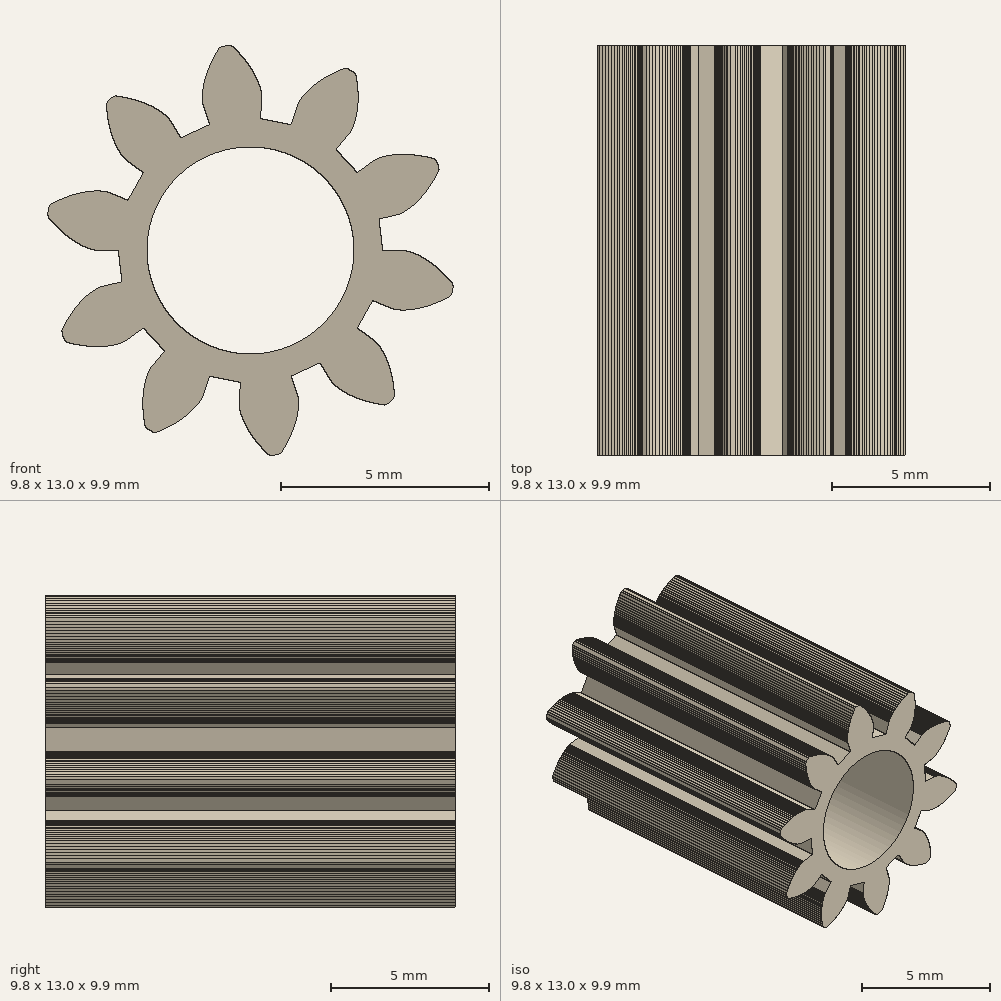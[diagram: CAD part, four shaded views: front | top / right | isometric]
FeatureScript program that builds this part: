
annotation { "Feature Type Name" : "Feature", "Feature Type Description" : "" }
export const myFeature = defineFeature(function(context is Context, id is Id, definition is map)
    precondition{}
    {
        {
            var Q0;
            Q0=qCreatedBy(makeId("Front.planeOp"),FACE);
            var sketch = newSketch(context, id + "F0", { "sketchPlane" : qUnion([Q0])});
            skCircle(sketch, "E0", {"center": v(0, 0) * mm, "radius": 2.5 * mm});
            skCircle(sketch, "E1", {"center": v(0, 0) * mm, "radius": 6 * mm});
            skLineSegment(sketch, "E2", {"start": v(3.6, 0.87) * mm, "end": v(3.1, 0.76) * mm});
            skLineSegment(sketch, "E3", {"start": v(3.6, 0.88) * mm, "end": v(3.6, 0.87) * mm});
            skLineSegment(sketch, "E4", {"start": v(3.6, 0.88) * mm, "end": v(3.6, 0.88) * mm});
            skLineSegment(sketch, "E5", {"start": v(3.62, 0.88) * mm, "end": v(3.6, 0.88) * mm});
            skLineSegment(sketch, "E6", {"start": v(3.63, 0.9) * mm, "end": v(3.62, 0.88) * mm});
            skLineSegment(sketch, "E7", {"start": v(3.65, 0.9) * mm, "end": v(3.63, 0.9) * mm});
            skLineSegment(sketch, "E8", {"start": v(3.68, 0.91) * mm, "end": v(3.65, 0.9) * mm});
            skLineSegment(sketch, "E9", {"start": v(3.7, 0.93) * mm, "end": v(3.68, 0.91) * mm});
            skLineSegment(sketch, "E10", {"start": v(3.74, 0.94) * mm, "end": v(3.7, 0.93) * mm});
            skLineSegment(sketch, "E11", {"start": v(3.77, 0.96) * mm, "end": v(3.74, 0.94) * mm});
            skLineSegment(sketch, "E12", {"start": v(3.8, 0.99) * mm, "end": v(3.77, 0.96) * mm});
            skLineSegment(sketch, "E13", {"start": v(3.85, 1.02) * mm, "end": v(3.8, 0.99) * mm});
            skLineSegment(sketch, "E14", {"start": v(3.9, 1.05) * mm, "end": v(3.85, 1.02) * mm});
            skLineSegment(sketch, "E15", {"start": v(3.94, 1.09) * mm, "end": v(3.9, 1.05) * mm});
            skLineSegment(sketch, "E16", {"start": v(3.98, 1.13) * mm, "end": v(3.94, 1.09) * mm});
            skLineSegment(sketch, "E17", {"start": v(4.03, 1.18) * mm, "end": v(3.98, 1.13) * mm});
            skLineSegment(sketch, "E18", {"start": v(4.08, 1.23) * mm, "end": v(4.03, 1.18) * mm});
            skLineSegment(sketch, "E19", {"start": v(4.14, 1.29) * mm, "end": v(4.08, 1.23) * mm});
            skLineSegment(sketch, "E20", {"start": v(4.19, 1.35) * mm, "end": v(4.14, 1.29) * mm});
            skLineSegment(sketch, "E21", {"start": v(4.24, 1.41) * mm, "end": v(4.19, 1.35) * mm});
            skLineSegment(sketch, "E22", {"start": v(4.3, 1.49) * mm, "end": v(4.24, 1.41) * mm});
            skLineSegment(sketch, "E23", {"start": v(4.35, 1.57) * mm, "end": v(4.3, 1.49) * mm});
            skLineSegment(sketch, "E24", {"start": v(4.4, 1.65) * mm, "end": v(4.35, 1.57) * mm});
            skLineSegment(sketch, "E25", {"start": v(4.45, 1.74) * mm, "end": v(4.4, 1.65) * mm});
            skLineSegment(sketch, "E26", {"start": v(4.5, 1.83) * mm, "end": v(4.45, 1.74) * mm});
            skLineSegment(sketch, "E27", {"start": v(4.55, 1.93) * mm, "end": v(4.5, 1.83) * mm});
            skLineSegment(sketch, "E28", {"start": v(4.55, 2.02) * mm, "end": v(4.55, 1.93) * mm});
            skLineSegment(sketch, "E29", {"start": v(4.48, 2.16) * mm, "end": v(4.55, 2.02) * mm});
            skLineSegment(sketch, "E30", {"start": v(4.42, 2.22) * mm, "end": v(4.48, 2.16) * mm});
            skLineSegment(sketch, "E31", {"start": v(4.31, 2.25) * mm, "end": v(4.42, 2.22) * mm});
            skLineSegment(sketch, "E32", {"start": v(4.2, 2.27) * mm, "end": v(4.31, 2.25) * mm});
            skLineSegment(sketch, "E33", {"start": v(4.1, 2.29) * mm, "end": v(4.2, 2.27) * mm});
            skLineSegment(sketch, "E34", {"start": v(4, 2.3) * mm, "end": v(4.1, 2.29) * mm});
            skLineSegment(sketch, "E35", {"start": v(3.91, 2.31) * mm, "end": v(4, 2.3) * mm});
            skLineSegment(sketch, "E36", {"start": v(3.82, 2.32) * mm, "end": v(3.91, 2.31) * mm});
            skLineSegment(sketch, "E37", {"start": v(3.74, 2.32) * mm, "end": v(3.82, 2.32) * mm});
            skLineSegment(sketch, "E38", {"start": v(3.66, 2.32) * mm, "end": v(3.74, 2.32) * mm});
            skLineSegment(sketch, "E39", {"start": v(3.58, 2.32) * mm, "end": v(3.66, 2.32) * mm});
            skLineSegment(sketch, "E40", {"start": v(3.5, 2.31) * mm, "end": v(3.58, 2.32) * mm});
            skLineSegment(sketch, "E41", {"start": v(3.44, 2.3) * mm, "end": v(3.5, 2.31) * mm});
            skLineSegment(sketch, "E42", {"start": v(3.38, 2.3) * mm, "end": v(3.44, 2.3) * mm});
            skLineSegment(sketch, "E43", {"start": v(3.32, 2.29) * mm, "end": v(3.38, 2.3) * mm});
            skLineSegment(sketch, "E44", {"start": v(3.27, 2.28) * mm, "end": v(3.32, 2.29) * mm});
            skLineSegment(sketch, "E45", {"start": v(3.22, 2.26) * mm, "end": v(3.27, 2.28) * mm});
            skLineSegment(sketch, "E46", {"start": v(3.18, 2.25) * mm, "end": v(3.22, 2.26) * mm});
            skLineSegment(sketch, "E47", {"start": v(3.14, 2.24) * mm, "end": v(3.18, 2.25) * mm});
            skLineSegment(sketch, "E48", {"start": v(3.1, 2.23) * mm, "end": v(3.14, 2.24) * mm});
            skLineSegment(sketch, "E49", {"start": v(3.07, 2.22) * mm, "end": v(3.1, 2.23) * mm});
            skLineSegment(sketch, "E50", {"start": v(3.05, 2.2) * mm, "end": v(3.07, 2.22) * mm});
            skLineSegment(sketch, "E51", {"start": v(3.03, 2.2) * mm, "end": v(3.05, 2.2) * mm});
            skLineSegment(sketch, "E52", {"start": v(3.01, 2.19) * mm, "end": v(3.03, 2.2) * mm});
            skLineSegment(sketch, "E53", {"start": v(3, 2.18) * mm, "end": v(3.01, 2.19) * mm});
            skLineSegment(sketch, "E54", {"start": v(3, 2.18) * mm, "end": v(3, 2.18) * mm});
            skLineSegment(sketch, "E55", {"start": v(3, 2.17) * mm, "end": v(3, 2.18) * mm});
            skLineSegment(sketch, "E56", {"start": v(2.58, 1.88) * mm, "end": v(3, 2.17) * mm});
            skLineSegment(sketch, "E57", {"start": v(2.07, 2.44) * mm, "end": v(2.58, 1.88) * mm});
            skLineSegment(sketch, "E58", {"start": v(2.4, 2.82) * mm, "end": v(2.07, 2.44) * mm});
            skLineSegment(sketch, "E59", {"start": v(2.4, 2.82) * mm, "end": v(2.4, 2.82) * mm});
            skLineSegment(sketch, "E60", {"start": v(2.4, 2.83) * mm, "end": v(2.4, 2.82) * mm});
            skLineSegment(sketch, "E61", {"start": v(2.4, 2.84) * mm, "end": v(2.4, 2.83) * mm});
            skLineSegment(sketch, "E62", {"start": v(2.42, 2.86) * mm, "end": v(2.4, 2.84) * mm});
            skLineSegment(sketch, "E63", {"start": v(2.43, 2.88) * mm, "end": v(2.42, 2.86) * mm});
            skLineSegment(sketch, "E64", {"start": v(2.44, 2.9) * mm, "end": v(2.43, 2.88) * mm});
            skLineSegment(sketch, "E65", {"start": v(2.45, 2.93) * mm, "end": v(2.44, 2.9) * mm});
            skLineSegment(sketch, "E66", {"start": v(2.47, 2.96) * mm, "end": v(2.45, 2.93) * mm});
            skLineSegment(sketch, "E67", {"start": v(2.48, 3) * mm, "end": v(2.47, 2.96) * mm});
            skLineSegment(sketch, "E68", {"start": v(2.5, 3.04) * mm, "end": v(2.48, 3) * mm});
            skLineSegment(sketch, "E69", {"start": v(2.52, 3.09) * mm, "end": v(2.5, 3.04) * mm});
            skLineSegment(sketch, "E70", {"start": v(2.53, 3.14) * mm, "end": v(2.52, 3.09) * mm});
            skLineSegment(sketch, "E71", {"start": v(2.55, 3.2) * mm, "end": v(2.53, 3.14) * mm});
            skLineSegment(sketch, "E72", {"start": v(2.56, 3.26) * mm, "end": v(2.55, 3.2) * mm});
            skLineSegment(sketch, "E73", {"start": v(2.57, 3.32) * mm, "end": v(2.56, 3.26) * mm});
            skLineSegment(sketch, "E74", {"start": v(2.58, 3.4) * mm, "end": v(2.57, 3.32) * mm});
            skLineSegment(sketch, "E75", {"start": v(2.59, 3.47) * mm, "end": v(2.58, 3.4) * mm});
            skLineSegment(sketch, "E76", {"start": v(2.6, 3.55) * mm, "end": v(2.59, 3.47) * mm});
            skLineSegment(sketch, "E77", {"start": v(2.6, 3.64) * mm, "end": v(2.6, 3.55) * mm});
            skLineSegment(sketch, "E78", {"start": v(2.6, 3.73) * mm, "end": v(2.6, 3.64) * mm});
            skLineSegment(sketch, "E79", {"start": v(2.6, 3.82) * mm, "end": v(2.6, 3.73) * mm});
            skLineSegment(sketch, "E80", {"start": v(2.6, 3.92) * mm, "end": v(2.6, 3.82) * mm});
            skLineSegment(sketch, "E81", {"start": v(2.58, 4.02) * mm, "end": v(2.6, 3.92) * mm});
            skLineSegment(sketch, "E82", {"start": v(2.57, 4.13) * mm, "end": v(2.58, 4.02) * mm});
            skLineSegment(sketch, "E83", {"start": v(2.55, 4.24) * mm, "end": v(2.57, 4.13) * mm});
            skLineSegment(sketch, "E84", {"start": v(2.5, 4.3) * mm, "end": v(2.55, 4.24) * mm});
            skLineSegment(sketch, "E85", {"start": v(2.35, 4.39) * mm, "end": v(2.5, 4.3) * mm});
            skLineSegment(sketch, "E86", {"start": v(2.27, 4.4) * mm, "end": v(2.35, 4.39) * mm});
            skLineSegment(sketch, "E87", {"start": v(2.17, 4.35) * mm, "end": v(2.27, 4.4) * mm});
            skLineSegment(sketch, "E88", {"start": v(2.07, 4.3) * mm, "end": v(2.17, 4.35) * mm});
            skLineSegment(sketch, "E89", {"start": v(1.98, 4.26) * mm, "end": v(2.07, 4.3) * mm});
            skLineSegment(sketch, "E90", {"start": v(1.89, 4.22) * mm, "end": v(1.98, 4.26) * mm});
            skLineSegment(sketch, "E91", {"start": v(1.8, 4.17) * mm, "end": v(1.89, 4.22) * mm});
            skLineSegment(sketch, "E92", {"start": v(1.73, 4.12) * mm, "end": v(1.8, 4.17) * mm});
            skLineSegment(sketch, "E93", {"start": v(1.66, 4.07) * mm, "end": v(1.73, 4.12) * mm});
            skLineSegment(sketch, "E94", {"start": v(1.6, 4.03) * mm, "end": v(1.66, 4.07) * mm});
            skLineSegment(sketch, "E95", {"start": v(1.53, 3.98) * mm, "end": v(1.6, 4.03) * mm});
            skLineSegment(sketch, "E96", {"start": v(1.48, 3.93) * mm, "end": v(1.53, 3.98) * mm});
            skLineSegment(sketch, "E97", {"start": v(1.43, 3.89) * mm, "end": v(1.48, 3.93) * mm});
            skLineSegment(sketch, "E98", {"start": v(1.38, 3.84) * mm, "end": v(1.43, 3.89) * mm});
            skLineSegment(sketch, "E99", {"start": v(1.34, 3.8) * mm, "end": v(1.38, 3.84) * mm});
            skLineSegment(sketch, "E100", {"start": v(1.3, 3.76) * mm, "end": v(1.34, 3.8) * mm});
            skLineSegment(sketch, "E101", {"start": v(1.27, 3.72) * mm, "end": v(1.3, 3.76) * mm});
            skLineSegment(sketch, "E102", {"start": v(1.25, 3.69) * mm, "end": v(1.27, 3.72) * mm});
            skLineSegment(sketch, "E103", {"start": v(1.22, 3.66) * mm, "end": v(1.25, 3.69) * mm});
            skLineSegment(sketch, "E104", {"start": v(1.2, 3.63) * mm, "end": v(1.22, 3.66) * mm});
            skLineSegment(sketch, "E105", {"start": v(1.18, 3.6) * mm, "end": v(1.2, 3.63) * mm});
            skLineSegment(sketch, "E106", {"start": v(1.17, 3.58) * mm, "end": v(1.18, 3.6) * mm});
            skLineSegment(sketch, "E107", {"start": v(1.16, 3.56) * mm, "end": v(1.17, 3.58) * mm});
            skLineSegment(sketch, "E108", {"start": v(1.15, 3.54) * mm, "end": v(1.16, 3.56) * mm});
            skLineSegment(sketch, "E109", {"start": v(1.15, 3.53) * mm, "end": v(1.15, 3.54) * mm});
            skLineSegment(sketch, "E110", {"start": v(1.14, 3.52) * mm, "end": v(1.15, 3.53) * mm});
            skLineSegment(sketch, "E111", {"start": v(1.14, 3.52) * mm, "end": v(1.14, 3.52) * mm});
            skLineSegment(sketch, "E112", {"start": v(0.99, 3.04) * mm, "end": v(1.14, 3.52) * mm});
            skLineSegment(sketch, "E113", {"start": v(0.24, 3.18) * mm, "end": v(0.99, 3.04) * mm});
            skLineSegment(sketch, "E114", {"start": v(0.28, 3.69) * mm, "end": v(0.24, 3.18) * mm});
            skLineSegment(sketch, "E115", {"start": v(0.28, 3.7) * mm, "end": v(0.28, 3.69) * mm});
            skLineSegment(sketch, "E116", {"start": v(0.28, 3.7) * mm, "end": v(0.28, 3.7) * mm});
            skLineSegment(sketch, "E117", {"start": v(0.28, 3.71) * mm, "end": v(0.28, 3.7) * mm});
            skLineSegment(sketch, "E118", {"start": v(0.28, 3.73) * mm, "end": v(0.28, 3.71) * mm});
            skLineSegment(sketch, "E119", {"start": v(0.27, 3.75) * mm, "end": v(0.28, 3.73) * mm});
            skLineSegment(sketch, "E120", {"start": v(0.27, 3.78) * mm, "end": v(0.27, 3.75) * mm});
            skLineSegment(sketch, "E121", {"start": v(0.27, 3.81) * mm, "end": v(0.27, 3.78) * mm});
            skLineSegment(sketch, "E122", {"start": v(0.26, 3.85) * mm, "end": v(0.27, 3.81) * mm});
            skLineSegment(sketch, "E123", {"start": v(0.25, 3.89) * mm, "end": v(0.26, 3.85) * mm});
            skLineSegment(sketch, "E124", {"start": v(0.24, 3.93) * mm, "end": v(0.25, 3.89) * mm});
            skLineSegment(sketch, "E125", {"start": v(0.22, 3.98) * mm, "end": v(0.24, 3.93) * mm});
            skLineSegment(sketch, "E126", {"start": v(0.2, 4.03) * mm, "end": v(0.22, 3.98) * mm});
            skLineSegment(sketch, "E127", {"start": v(0.18, 4.08) * mm, "end": v(0.2, 4.03) * mm});
            skLineSegment(sketch, "E128", {"start": v(0.16, 4.14) * mm, "end": v(0.18, 4.08) * mm});
            skLineSegment(sketch, "E129", {"start": v(0.13, 4.2) * mm, "end": v(0.16, 4.14) * mm});
            skLineSegment(sketch, "E130", {"start": v(0.1, 4.26) * mm, "end": v(0.13, 4.2) * mm});
            skLineSegment(sketch, "E131", {"start": v(0.05, 4.33) * mm, "end": v(0.1, 4.26) * mm});
            skLineSegment(sketch, "E132", {"start": v(0.01, 4.4) * mm, "end": v(0.05, 4.33) * mm});
            skLineSegment(sketch, "E133", {"start": v(-0.04, 4.47) * mm, "end": v(0.01, 4.4) * mm});
            skLineSegment(sketch, "E134", {"start": v(-0.09, 4.54) * mm, "end": v(-0.04, 4.47) * mm});
            skLineSegment(sketch, "E135", {"start": v(-0.15, 4.62) * mm, "end": v(-0.09, 4.54) * mm});
            skLineSegment(sketch, "E136", {"start": v(-0.2, 4.7) * mm, "end": v(-0.15, 4.62) * mm});
            skLineSegment(sketch, "E137", {"start": v(-0.28, 4.77) * mm, "end": v(-0.2, 4.7) * mm});
            skLineSegment(sketch, "E138", {"start": v(-0.35, 4.85) * mm, "end": v(-0.28, 4.77) * mm});
            skLineSegment(sketch, "E139", {"start": v(-0.43, 4.93) * mm, "end": v(-0.35, 4.85) * mm});
            skLineSegment(sketch, "E140", {"start": v(-0.51, 4.95) * mm, "end": v(-0.43, 4.93) * mm});
            skLineSegment(sketch, "E141", {"start": v(-0.67, 4.93) * mm, "end": v(-0.51, 4.95) * mm});
            skLineSegment(sketch, "E142", {"start": v(-0.75, 4.9) * mm, "end": v(-0.67, 4.93) * mm});
            skLineSegment(sketch, "E143", {"start": v(-0.8, 4.8) * mm, "end": v(-0.75, 4.9) * mm});
            skLineSegment(sketch, "E144", {"start": v(-0.86, 4.7) * mm, "end": v(-0.8, 4.8) * mm});
            skLineSegment(sketch, "E145", {"start": v(-0.9, 4.61) * mm, "end": v(-0.86, 4.7) * mm});
            skLineSegment(sketch, "E146", {"start": v(-0.95, 4.52) * mm, "end": v(-0.9, 4.61) * mm});
            skLineSegment(sketch, "E147", {"start": v(-1, 4.44) * mm, "end": v(-0.95, 4.52) * mm});
            skLineSegment(sketch, "E148", {"start": v(-1.02, 4.35) * mm, "end": v(-1, 4.44) * mm});
            skLineSegment(sketch, "E149", {"start": v(-1.05, 4.27) * mm, "end": v(-1.02, 4.35) * mm});
            skLineSegment(sketch, "E150", {"start": v(-1.08, 4.2) * mm, "end": v(-1.05, 4.27) * mm});
            skLineSegment(sketch, "E151", {"start": v(-1.1, 4.12) * mm, "end": v(-1.08, 4.2) * mm});
            skLineSegment(sketch, "E152", {"start": v(-1.12, 4.05) * mm, "end": v(-1.1, 4.12) * mm});
            skLineSegment(sketch, "E153", {"start": v(-1.13, 3.98) * mm, "end": v(-1.12, 4.05) * mm});
            skLineSegment(sketch, "E154", {"start": v(-1.14, 3.92) * mm, "end": v(-1.13, 3.98) * mm});
            skLineSegment(sketch, "E155", {"start": v(-1.15, 3.86) * mm, "end": v(-1.14, 3.92) * mm});
            skLineSegment(sketch, "E156", {"start": v(-1.16, 3.81) * mm, "end": v(-1.15, 3.86) * mm});
            skLineSegment(sketch, "E157", {"start": v(-1.16, 3.76) * mm, "end": v(-1.16, 3.81) * mm});
            skLineSegment(sketch, "E158", {"start": v(-1.16, 3.72) * mm, "end": v(-1.16, 3.76) * mm});
            skLineSegment(sketch, "E159", {"start": v(-1.16, 3.68) * mm, "end": v(-1.16, 3.72) * mm});
            skLineSegment(sketch, "E160", {"start": v(-1.16, 3.64) * mm, "end": v(-1.16, 3.68) * mm});
            skLineSegment(sketch, "E161", {"start": v(-1.16, 3.6) * mm, "end": v(-1.16, 3.64) * mm});
            skLineSegment(sketch, "E162", {"start": v(-1.15, 3.58) * mm, "end": v(-1.16, 3.6) * mm});
            skLineSegment(sketch, "E163", {"start": v(-1.15, 3.56) * mm, "end": v(-1.15, 3.58) * mm});
            skLineSegment(sketch, "E164", {"start": v(-1.15, 3.54) * mm, "end": v(-1.15, 3.56) * mm});
            skLineSegment(sketch, "E165", {"start": v(-1.15, 3.53) * mm, "end": v(-1.15, 3.54) * mm});
            skLineSegment(sketch, "E166", {"start": v(-1.14, 3.52) * mm, "end": v(-1.15, 3.53) * mm});
            skLineSegment(sketch, "E167", {"start": v(-1.14, 3.52) * mm, "end": v(-1.14, 3.52) * mm});
            skLineSegment(sketch, "E168", {"start": v(-0.99, 3.04) * mm, "end": v(-1.14, 3.52) * mm});
            skLineSegment(sketch, "E169", {"start": v(-1.68, 2.72) * mm, "end": v(-0.99, 3.04) * mm});
            skLineSegment(sketch, "E170", {"start": v(-1.94, 3.15) * mm, "end": v(-1.68, 2.72) * mm});
            skLineSegment(sketch, "E171", {"start": v(-1.94, 3.15) * mm, "end": v(-1.94, 3.15) * mm});
            skLineSegment(sketch, "E172", {"start": v(-1.95, 3.16) * mm, "end": v(-1.94, 3.15) * mm});
            skLineSegment(sketch, "E173", {"start": v(-1.96, 3.17) * mm, "end": v(-1.95, 3.16) * mm});
            skLineSegment(sketch, "E174", {"start": v(-1.97, 3.18) * mm, "end": v(-1.96, 3.17) * mm});
            skLineSegment(sketch, "E175", {"start": v(-1.98, 3.2) * mm, "end": v(-1.97, 3.18) * mm});
            skLineSegment(sketch, "E176", {"start": v(-2, 3.22) * mm, "end": v(-1.98, 3.2) * mm});
            skLineSegment(sketch, "E177", {"start": v(-2.03, 3.24) * mm, "end": v(-2, 3.22) * mm});
            skLineSegment(sketch, "E178", {"start": v(-2.05, 3.26) * mm, "end": v(-2.03, 3.24) * mm});
            skLineSegment(sketch, "E179", {"start": v(-2.08, 3.29) * mm, "end": v(-2.05, 3.26) * mm});
            skLineSegment(sketch, "E180", {"start": v(-2.12, 3.32) * mm, "end": v(-2.08, 3.29) * mm});
            skLineSegment(sketch, "E181", {"start": v(-2.16, 3.35) * mm, "end": v(-2.12, 3.32) * mm});
            skLineSegment(sketch, "E182", {"start": v(-2.2, 3.38) * mm, "end": v(-2.16, 3.35) * mm});
            skLineSegment(sketch, "E183", {"start": v(-2.25, 3.4) * mm, "end": v(-2.2, 3.38) * mm});
            skLineSegment(sketch, "E184", {"start": v(-2.3, 3.44) * mm, "end": v(-2.25, 3.4) * mm});
            skLineSegment(sketch, "E185", {"start": v(-2.37, 3.47) * mm, "end": v(-2.3, 3.44) * mm});
            skLineSegment(sketch, "E186", {"start": v(-2.43, 3.5) * mm, "end": v(-2.37, 3.47) * mm});
            skLineSegment(sketch, "E187", {"start": v(-2.5, 3.54) * mm, "end": v(-2.43, 3.5) * mm});
            skLineSegment(sketch, "E188", {"start": v(-2.58, 3.57) * mm, "end": v(-2.5, 3.54) * mm});
            skLineSegment(sketch, "E189", {"start": v(-2.66, 3.6) * mm, "end": v(-2.58, 3.57) * mm});
            skLineSegment(sketch, "E190", {"start": v(-2.74, 3.62) * mm, "end": v(-2.66, 3.6) * mm});
            skLineSegment(sketch, "E191", {"start": v(-2.83, 3.65) * mm, "end": v(-2.74, 3.62) * mm});
            skLineSegment(sketch, "E192", {"start": v(-2.93, 3.68) * mm, "end": v(-2.83, 3.65) * mm});
            skLineSegment(sketch, "E193", {"start": v(-3.03, 3.7) * mm, "end": v(-2.93, 3.68) * mm});
            skLineSegment(sketch, "E194", {"start": v(-3.14, 3.72) * mm, "end": v(-3.03, 3.7) * mm});
            skLineSegment(sketch, "E195", {"start": v(-3.25, 3.73) * mm, "end": v(-3.14, 3.72) * mm});
            skLineSegment(sketch, "E196", {"start": v(-3.33, 3.7) * mm, "end": v(-3.25, 3.73) * mm});
            skLineSegment(sketch, "E197", {"start": v(-3.44, 3.6) * mm, "end": v(-3.33, 3.7) * mm});
            skLineSegment(sketch, "E198", {"start": v(-3.48, 3.52) * mm, "end": v(-3.44, 3.6) * mm});
            skLineSegment(sketch, "E199", {"start": v(-3.47, 3.4) * mm, "end": v(-3.48, 3.52) * mm});
            skLineSegment(sketch, "E200", {"start": v(-3.46, 3.3) * mm, "end": v(-3.47, 3.4) * mm});
            skLineSegment(sketch, "E201", {"start": v(-3.45, 3.2) * mm, "end": v(-3.46, 3.3) * mm});
            skLineSegment(sketch, "E202", {"start": v(-3.43, 3.1) * mm, "end": v(-3.45, 3.2) * mm});
            skLineSegment(sketch, "E203", {"start": v(-3.4, 3) * mm, "end": v(-3.43, 3.1) * mm});
            skLineSegment(sketch, "E204", {"start": v(-3.39, 2.92) * mm, "end": v(-3.4, 3) * mm});
            skLineSegment(sketch, "E205", {"start": v(-3.36, 2.84) * mm, "end": v(-3.39, 2.92) * mm});
            skLineSegment(sketch, "E206", {"start": v(-3.34, 2.76) * mm, "end": v(-3.36, 2.84) * mm});
            skLineSegment(sketch, "E207", {"start": v(-3.31, 2.69) * mm, "end": v(-3.34, 2.76) * mm});
            skLineSegment(sketch, "E208", {"start": v(-3.28, 2.62) * mm, "end": v(-3.31, 2.69) * mm});
            skLineSegment(sketch, "E209", {"start": v(-3.26, 2.56) * mm, "end": v(-3.28, 2.62) * mm});
            skLineSegment(sketch, "E210", {"start": v(-3.23, 2.5) * mm, "end": v(-3.26, 2.56) * mm});
            skLineSegment(sketch, "E211", {"start": v(-3.2, 2.45) * mm, "end": v(-3.23, 2.5) * mm});
            skLineSegment(sketch, "E212", {"start": v(-3.18, 2.4) * mm, "end": v(-3.2, 2.45) * mm});
            skLineSegment(sketch, "E213", {"start": v(-3.15, 2.36) * mm, "end": v(-3.18, 2.4) * mm});
            skLineSegment(sketch, "E214", {"start": v(-3.12, 2.32) * mm, "end": v(-3.15, 2.36) * mm});
            skLineSegment(sketch, "E215", {"start": v(-3.1, 2.3) * mm, "end": v(-3.12, 2.32) * mm});
            skLineSegment(sketch, "E216", {"start": v(-3.08, 2.26) * mm, "end": v(-3.1, 2.3) * mm});
            skLineSegment(sketch, "E217", {"start": v(-3.06, 2.24) * mm, "end": v(-3.08, 2.26) * mm});
            skLineSegment(sketch, "E218", {"start": v(-3.04, 2.22) * mm, "end": v(-3.06, 2.24) * mm});
            skLineSegment(sketch, "E219", {"start": v(-3.02, 2.2) * mm, "end": v(-3.04, 2.22) * mm});
            skLineSegment(sketch, "E220", {"start": v(-3.01, 2.2) * mm, "end": v(-3.02, 2.2) * mm});
            skLineSegment(sketch, "E221", {"start": v(-3, 2.18) * mm, "end": v(-3.01, 2.2) * mm});
            skLineSegment(sketch, "E222", {"start": v(-3, 2.18) * mm, "end": v(-3, 2.18) * mm});
            skLineSegment(sketch, "E223", {"start": v(-3, 2.17) * mm, "end": v(-3, 2.18) * mm});
            skLineSegment(sketch, "E224", {"start": v(-2.58, 1.88) * mm, "end": v(-3, 2.17) * mm});
            skLineSegment(sketch, "E225", {"start": v(-2.95, 1.21) * mm, "end": v(-2.58, 1.88) * mm});
            skLineSegment(sketch, "E226", {"start": v(-3.42, 1.4) * mm, "end": v(-2.95, 1.21) * mm});
            skLineSegment(sketch, "E227", {"start": v(-3.42, 1.4) * mm, "end": v(-3.42, 1.4) * mm});
            skLineSegment(sketch, "E228", {"start": v(-3.43, 1.4) * mm, "end": v(-3.42, 1.4) * mm});
            skLineSegment(sketch, "E229", {"start": v(-3.45, 1.41) * mm, "end": v(-3.43, 1.4) * mm});
            skLineSegment(sketch, "E230", {"start": v(-3.46, 1.42) * mm, "end": v(-3.45, 1.41) * mm});
            skLineSegment(sketch, "E231", {"start": v(-3.48, 1.42) * mm, "end": v(-3.46, 1.42) * mm});
            skLineSegment(sketch, "E232", {"start": v(-3.51, 1.43) * mm, "end": v(-3.48, 1.42) * mm});
            skLineSegment(sketch, "E233", {"start": v(-3.54, 1.43) * mm, "end": v(-3.51, 1.43) * mm});
            skLineSegment(sketch, "E234", {"start": v(-3.58, 1.43) * mm, "end": v(-3.54, 1.43) * mm});
            skLineSegment(sketch, "E235", {"start": v(-3.62, 1.44) * mm, "end": v(-3.58, 1.43) * mm});
            skLineSegment(sketch, "E236", {"start": v(-3.66, 1.44) * mm, "end": v(-3.62, 1.44) * mm});
            skLineSegment(sketch, "E237", {"start": v(-3.71, 1.44) * mm, "end": v(-3.66, 1.44) * mm});
            skLineSegment(sketch, "E238", {"start": v(-3.77, 1.44) * mm, "end": v(-3.71, 1.44) * mm});
            skLineSegment(sketch, "E239", {"start": v(-3.83, 1.43) * mm, "end": v(-3.77, 1.44) * mm});
            skLineSegment(sketch, "E240", {"start": v(-3.89, 1.43) * mm, "end": v(-3.83, 1.43) * mm});
            skLineSegment(sketch, "E241", {"start": v(-3.96, 1.42) * mm, "end": v(-3.89, 1.43) * mm});
            skLineSegment(sketch, "E242", {"start": v(-4.03, 1.4) * mm, "end": v(-3.96, 1.42) * mm});
            skLineSegment(sketch, "E243", {"start": v(-4.1, 1.4) * mm, "end": v(-4.03, 1.4) * mm});
            skLineSegment(sketch, "E244", {"start": v(-4.18, 1.37) * mm, "end": v(-4.1, 1.4) * mm});
            skLineSegment(sketch, "E245", {"start": v(-4.26, 1.35) * mm, "end": v(-4.18, 1.37) * mm});
            skLineSegment(sketch, "E246", {"start": v(-4.35, 1.32) * mm, "end": v(-4.26, 1.35) * mm});
            skLineSegment(sketch, "E247", {"start": v(-4.44, 1.29) * mm, "end": v(-4.35, 1.32) * mm});
            skLineSegment(sketch, "E248", {"start": v(-4.53, 1.25) * mm, "end": v(-4.44, 1.29) * mm});
            skLineSegment(sketch, "E249", {"start": v(-4.62, 1.21) * mm, "end": v(-4.53, 1.25) * mm});
            skLineSegment(sketch, "E250", {"start": v(-4.72, 1.16) * mm, "end": v(-4.62, 1.21) * mm});
            skLineSegment(sketch, "E251", {"start": v(-4.82, 1.11) * mm, "end": v(-4.72, 1.16) * mm});
            skLineSegment(sketch, "E252", {"start": v(-4.87, 1.04) * mm, "end": v(-4.82, 1.11) * mm});
            skLineSegment(sketch, "E253", {"start": v(-4.9, 0.88) * mm, "end": v(-4.87, 1.04) * mm});
            skLineSegment(sketch, "E254", {"start": v(-4.88, 0.8) * mm, "end": v(-4.9, 0.88) * mm});
            skLineSegment(sketch, "E255", {"start": v(-4.8, 0.72) * mm, "end": v(-4.88, 0.8) * mm});
            skLineSegment(sketch, "E256", {"start": v(-4.74, 0.64) * mm, "end": v(-4.8, 0.72) * mm});
            skLineSegment(sketch, "E257", {"start": v(-4.67, 0.56) * mm, "end": v(-4.74, 0.64) * mm});
            skLineSegment(sketch, "E258", {"start": v(-4.6, 0.5) * mm, "end": v(-4.67, 0.56) * mm});
            skLineSegment(sketch, "E259", {"start": v(-4.52, 0.43) * mm, "end": v(-4.6, 0.5) * mm});
            skLineSegment(sketch, "E260", {"start": v(-4.46, 0.37) * mm, "end": v(-4.52, 0.43) * mm});
            skLineSegment(sketch, "E261", {"start": v(-4.39, 0.32) * mm, "end": v(-4.46, 0.37) * mm});
            skLineSegment(sketch, "E262", {"start": v(-4.32, 0.27) * mm, "end": v(-4.39, 0.32) * mm});
            skLineSegment(sketch, "E263", {"start": v(-4.26, 0.23) * mm, "end": v(-4.32, 0.27) * mm});
            skLineSegment(sketch, "E264", {"start": v(-4.2, 0.19) * mm, "end": v(-4.26, 0.23) * mm});
            skLineSegment(sketch, "E265", {"start": v(-4.14, 0.16) * mm, "end": v(-4.2, 0.19) * mm});
            skLineSegment(sketch, "E266", {"start": v(-4.08, 0.13) * mm, "end": v(-4.14, 0.16) * mm});
            skLineSegment(sketch, "E267", {"start": v(-4.03, 0.1) * mm, "end": v(-4.08, 0.13) * mm});
            skLineSegment(sketch, "E268", {"start": v(-3.98, 0.08) * mm, "end": v(-4.03, 0.1) * mm});
            skLineSegment(sketch, "E269", {"start": v(-3.94, 0.06) * mm, "end": v(-3.98, 0.08) * mm});
            skLineSegment(sketch, "E270", {"start": v(-3.9, 0.04) * mm, "end": v(-3.94, 0.06) * mm});
            skLineSegment(sketch, "E271", {"start": v(-3.85, 0.03) * mm, "end": v(-3.9, 0.04) * mm});
            skLineSegment(sketch, "E272", {"start": v(-3.82, 0.02) * mm, "end": v(-3.85, 0.03) * mm});
            skLineSegment(sketch, "E273", {"start": v(-3.79, 0.01) * mm, "end": v(-3.82, 0.02) * mm});
            skLineSegment(sketch, "E274", {"start": v(-3.76, 0) * mm, "end": v(-3.79, 0.01) * mm});
            skLineSegment(sketch, "E275", {"start": v(-3.74, 0) * mm, "end": v(-3.76, 0) * mm});
            skLineSegment(sketch, "E276", {"start": v(-3.72, 0) * mm, "end": v(-3.74, 0) * mm});
            skLineSegment(sketch, "E277", {"start": v(-3.7, 0) * mm, "end": v(-3.72, 0) * mm});
            skLineSegment(sketch, "E278", {"start": v(-3.7, 0) * mm, "end": v(-3.7, 0) * mm});
            skLineSegment(sketch, "E279", {"start": v(-3.2, 0) * mm, "end": v(-3.7, 0) * mm});
            skLineSegment(sketch, "E280", {"start": v(-3.1, -0.76) * mm, "end": v(-3.2, 0) * mm});
            skLineSegment(sketch, "E281", {"start": v(-3.6, -0.87) * mm, "end": v(-3.1, -0.76) * mm});
            skLineSegment(sketch, "E282", {"start": v(-3.6, -0.88) * mm, "end": v(-3.6, -0.87) * mm});
            skLineSegment(sketch, "E283", {"start": v(-3.6, -0.88) * mm, "end": v(-3.6, -0.88) * mm});
            skLineSegment(sketch, "E284", {"start": v(-3.62, -0.88) * mm, "end": v(-3.6, -0.88) * mm});
            skLineSegment(sketch, "E285", {"start": v(-3.63, -0.9) * mm, "end": v(-3.62, -0.88) * mm});
            skLineSegment(sketch, "E286", {"start": v(-3.65, -0.9) * mm, "end": v(-3.63, -0.9) * mm});
            skLineSegment(sketch, "E287", {"start": v(-3.68, -0.91) * mm, "end": v(-3.65, -0.9) * mm});
            skLineSegment(sketch, "E288", {"start": v(-3.7, -0.93) * mm, "end": v(-3.68, -0.91) * mm});
            skLineSegment(sketch, "E289", {"start": v(-3.74, -0.94) * mm, "end": v(-3.7, -0.93) * mm});
            skLineSegment(sketch, "E290", {"start": v(-3.77, -0.96) * mm, "end": v(-3.74, -0.94) * mm});
            skLineSegment(sketch, "E291", {"start": v(-3.8, -0.99) * mm, "end": v(-3.77, -0.96) * mm});
            skLineSegment(sketch, "E292", {"start": v(-3.85, -1.02) * mm, "end": v(-3.8, -0.99) * mm});
            skLineSegment(sketch, "E293", {"start": v(-3.9, -1.05) * mm, "end": v(-3.85, -1.02) * mm});
            skLineSegment(sketch, "E294", {"start": v(-3.94, -1.09) * mm, "end": v(-3.9, -1.05) * mm});
            skLineSegment(sketch, "E295", {"start": v(-3.98, -1.13) * mm, "end": v(-3.94, -1.09) * mm});
            skLineSegment(sketch, "E296", {"start": v(-4.03, -1.18) * mm, "end": v(-3.98, -1.13) * mm});
            skLineSegment(sketch, "E297", {"start": v(-4.08, -1.23) * mm, "end": v(-4.03, -1.18) * mm});
            skLineSegment(sketch, "E298", {"start": v(-4.14, -1.29) * mm, "end": v(-4.08, -1.23) * mm});
            skLineSegment(sketch, "E299", {"start": v(-4.19, -1.35) * mm, "end": v(-4.14, -1.29) * mm});
            skLineSegment(sketch, "E300", {"start": v(-4.24, -1.41) * mm, "end": v(-4.19, -1.35) * mm});
            skLineSegment(sketch, "E301", {"start": v(-4.3, -1.49) * mm, "end": v(-4.24, -1.41) * mm});
            skLineSegment(sketch, "E302", {"start": v(-4.35, -1.57) * mm, "end": v(-4.3, -1.49) * mm});
            skLineSegment(sketch, "E303", {"start": v(-4.4, -1.65) * mm, "end": v(-4.35, -1.57) * mm});
            skLineSegment(sketch, "E304", {"start": v(-4.45, -1.74) * mm, "end": v(-4.4, -1.65) * mm});
            skLineSegment(sketch, "E305", {"start": v(-4.5, -1.83) * mm, "end": v(-4.45, -1.74) * mm});
            skLineSegment(sketch, "E306", {"start": v(-4.55, -1.93) * mm, "end": v(-4.5, -1.83) * mm});
            skLineSegment(sketch, "E307", {"start": v(-4.55, -2.02) * mm, "end": v(-4.55, -1.93) * mm});
            skLineSegment(sketch, "E308", {"start": v(-4.48, -2.16) * mm, "end": v(-4.55, -2.02) * mm});
            skLineSegment(sketch, "E309", {"start": v(-4.42, -2.22) * mm, "end": v(-4.48, -2.16) * mm});
            skLineSegment(sketch, "E310", {"start": v(-4.31, -2.25) * mm, "end": v(-4.42, -2.22) * mm});
            skLineSegment(sketch, "E311", {"start": v(-4.2, -2.27) * mm, "end": v(-4.31, -2.25) * mm});
            skLineSegment(sketch, "E312", {"start": v(-4.1, -2.29) * mm, "end": v(-4.2, -2.27) * mm});
            skLineSegment(sketch, "E313", {"start": v(-4, -2.3) * mm, "end": v(-4.1, -2.29) * mm});
            skLineSegment(sketch, "E314", {"start": v(-3.91, -2.31) * mm, "end": v(-4, -2.3) * mm});
            skLineSegment(sketch, "E315", {"start": v(-3.82, -2.32) * mm, "end": v(-3.91, -2.31) * mm});
            skLineSegment(sketch, "E316", {"start": v(-3.74, -2.32) * mm, "end": v(-3.82, -2.32) * mm});
            skLineSegment(sketch, "E317", {"start": v(-3.66, -2.32) * mm, "end": v(-3.74, -2.32) * mm});
            skLineSegment(sketch, "E318", {"start": v(-3.58, -2.32) * mm, "end": v(-3.66, -2.32) * mm});
            skLineSegment(sketch, "E319", {"start": v(-3.5, -2.31) * mm, "end": v(-3.58, -2.32) * mm});
            skLineSegment(sketch, "E320", {"start": v(-3.44, -2.3) * mm, "end": v(-3.5, -2.31) * mm});
            skLineSegment(sketch, "E321", {"start": v(-3.38, -2.3) * mm, "end": v(-3.44, -2.3) * mm});
            skLineSegment(sketch, "E322", {"start": v(-3.32, -2.29) * mm, "end": v(-3.38, -2.3) * mm});
            skLineSegment(sketch, "E323", {"start": v(-3.27, -2.28) * mm, "end": v(-3.32, -2.29) * mm});
            skLineSegment(sketch, "E324", {"start": v(-3.22, -2.26) * mm, "end": v(-3.27, -2.28) * mm});
            skLineSegment(sketch, "E325", {"start": v(-3.18, -2.25) * mm, "end": v(-3.22, -2.26) * mm});
            skLineSegment(sketch, "E326", {"start": v(-3.14, -2.24) * mm, "end": v(-3.18, -2.25) * mm});
            skLineSegment(sketch, "E327", {"start": v(-3.1, -2.23) * mm, "end": v(-3.14, -2.24) * mm});
            skLineSegment(sketch, "E328", {"start": v(-3.07, -2.22) * mm, "end": v(-3.1, -2.23) * mm});
            skLineSegment(sketch, "E329", {"start": v(-3.05, -2.2) * mm, "end": v(-3.07, -2.22) * mm});
            skLineSegment(sketch, "E330", {"start": v(-3.03, -2.2) * mm, "end": v(-3.05, -2.2) * mm});
            skLineSegment(sketch, "E331", {"start": v(-3.01, -2.19) * mm, "end": v(-3.03, -2.2) * mm});
            skLineSegment(sketch, "E332", {"start": v(-3, -2.18) * mm, "end": v(-3.01, -2.19) * mm});
            skLineSegment(sketch, "E333", {"start": v(-3, -2.18) * mm, "end": v(-3, -2.18) * mm});
            skLineSegment(sketch, "E334", {"start": v(-3, -2.17) * mm, "end": v(-3, -2.18) * mm});
            skLineSegment(sketch, "E335", {"start": v(-2.58, -1.88) * mm, "end": v(-3, -2.17) * mm});
            skLineSegment(sketch, "E336", {"start": v(-2.07, -2.44) * mm, "end": v(-2.58, -1.88) * mm});
            skLineSegment(sketch, "E337", {"start": v(-2.4, -2.82) * mm, "end": v(-2.07, -2.44) * mm});
            skLineSegment(sketch, "E338", {"start": v(-2.4, -2.82) * mm, "end": v(-2.4, -2.82) * mm});
            skLineSegment(sketch, "E339", {"start": v(-2.4, -2.83) * mm, "end": v(-2.4, -2.82) * mm});
            skLineSegment(sketch, "E340", {"start": v(-2.4, -2.84) * mm, "end": v(-2.4, -2.83) * mm});
            skLineSegment(sketch, "E341", {"start": v(-2.42, -2.86) * mm, "end": v(-2.4, -2.84) * mm});
            skLineSegment(sketch, "E342", {"start": v(-2.43, -2.88) * mm, "end": v(-2.42, -2.86) * mm});
            skLineSegment(sketch, "E343", {"start": v(-2.44, -2.9) * mm, "end": v(-2.43, -2.88) * mm});
            skLineSegment(sketch, "E344", {"start": v(-2.45, -2.93) * mm, "end": v(-2.44, -2.9) * mm});
            skLineSegment(sketch, "E345", {"start": v(-2.47, -2.96) * mm, "end": v(-2.45, -2.93) * mm});
            skLineSegment(sketch, "E346", {"start": v(-2.48, -3) * mm, "end": v(-2.47, -2.96) * mm});
            skLineSegment(sketch, "E347", {"start": v(-2.5, -3.04) * mm, "end": v(-2.48, -3) * mm});
            skLineSegment(sketch, "E348", {"start": v(-2.52, -3.09) * mm, "end": v(-2.5, -3.04) * mm});
            skLineSegment(sketch, "E349", {"start": v(-2.53, -3.14) * mm, "end": v(-2.52, -3.09) * mm});
            skLineSegment(sketch, "E350", {"start": v(-2.55, -3.2) * mm, "end": v(-2.53, -3.14) * mm});
            skLineSegment(sketch, "E351", {"start": v(-2.56, -3.26) * mm, "end": v(-2.55, -3.2) * mm});
            skLineSegment(sketch, "E352", {"start": v(-2.57, -3.32) * mm, "end": v(-2.56, -3.26) * mm});
            skLineSegment(sketch, "E353", {"start": v(-2.58, -3.4) * mm, "end": v(-2.57, -3.32) * mm});
            skLineSegment(sketch, "E354", {"start": v(-2.59, -3.47) * mm, "end": v(-2.58, -3.4) * mm});
            skLineSegment(sketch, "E355", {"start": v(-2.6, -3.55) * mm, "end": v(-2.59, -3.47) * mm});
            skLineSegment(sketch, "E356", {"start": v(-2.6, -3.64) * mm, "end": v(-2.6, -3.55) * mm});
            skLineSegment(sketch, "E357", {"start": v(-2.6, -3.73) * mm, "end": v(-2.6, -3.64) * mm});
            skLineSegment(sketch, "E358", {"start": v(-2.6, -3.82) * mm, "end": v(-2.6, -3.73) * mm});
            skLineSegment(sketch, "E359", {"start": v(-2.6, -3.92) * mm, "end": v(-2.6, -3.82) * mm});
            skLineSegment(sketch, "E360", {"start": v(-2.58, -4.02) * mm, "end": v(-2.6, -3.92) * mm});
            skLineSegment(sketch, "E361", {"start": v(-2.57, -4.13) * mm, "end": v(-2.58, -4.02) * mm});
            skLineSegment(sketch, "E362", {"start": v(-2.55, -4.24) * mm, "end": v(-2.57, -4.13) * mm});
            skLineSegment(sketch, "E363", {"start": v(-2.5, -4.3) * mm, "end": v(-2.55, -4.24) * mm});
            skLineSegment(sketch, "E364", {"start": v(-2.35, -4.39) * mm, "end": v(-2.5, -4.3) * mm});
            skLineSegment(sketch, "E365", {"start": v(-2.27, -4.4) * mm, "end": v(-2.35, -4.39) * mm});
            skLineSegment(sketch, "E366", {"start": v(-2.17, -4.35) * mm, "end": v(-2.27, -4.4) * mm});
            skLineSegment(sketch, "E367", {"start": v(-2.07, -4.3) * mm, "end": v(-2.17, -4.35) * mm});
            skLineSegment(sketch, "E368", {"start": v(-1.98, -4.26) * mm, "end": v(-2.07, -4.3) * mm});
            skLineSegment(sketch, "E369", {"start": v(-1.89, -4.22) * mm, "end": v(-1.98, -4.26) * mm});
            skLineSegment(sketch, "E370", {"start": v(-1.8, -4.17) * mm, "end": v(-1.89, -4.22) * mm});
            skLineSegment(sketch, "E371", {"start": v(-1.73, -4.12) * mm, "end": v(-1.8, -4.17) * mm});
            skLineSegment(sketch, "E372", {"start": v(-1.66, -4.07) * mm, "end": v(-1.73, -4.12) * mm});
            skLineSegment(sketch, "E373", {"start": v(-1.6, -4.03) * mm, "end": v(-1.66, -4.07) * mm});
            skLineSegment(sketch, "E374", {"start": v(-1.53, -3.98) * mm, "end": v(-1.6, -4.03) * mm});
            skLineSegment(sketch, "E375", {"start": v(-1.48, -3.93) * mm, "end": v(-1.53, -3.98) * mm});
            skLineSegment(sketch, "E376", {"start": v(-1.43, -3.89) * mm, "end": v(-1.48, -3.93) * mm});
            skLineSegment(sketch, "E377", {"start": v(-1.38, -3.84) * mm, "end": v(-1.43, -3.89) * mm});
            skLineSegment(sketch, "E378", {"start": v(-1.34, -3.8) * mm, "end": v(-1.38, -3.84) * mm});
            skLineSegment(sketch, "E379", {"start": v(-1.3, -3.76) * mm, "end": v(-1.34, -3.8) * mm});
            skLineSegment(sketch, "E380", {"start": v(-1.27, -3.72) * mm, "end": v(-1.3, -3.76) * mm});
            skLineSegment(sketch, "E381", {"start": v(-1.25, -3.69) * mm, "end": v(-1.27, -3.72) * mm});
            skLineSegment(sketch, "E382", {"start": v(-1.22, -3.66) * mm, "end": v(-1.25, -3.69) * mm});
            skLineSegment(sketch, "E383", {"start": v(-1.2, -3.63) * mm, "end": v(-1.22, -3.66) * mm});
            skLineSegment(sketch, "E384", {"start": v(-1.18, -3.6) * mm, "end": v(-1.2, -3.63) * mm});
            skLineSegment(sketch, "E385", {"start": v(-1.17, -3.58) * mm, "end": v(-1.18, -3.6) * mm});
            skLineSegment(sketch, "E386", {"start": v(-1.16, -3.56) * mm, "end": v(-1.17, -3.58) * mm});
            skLineSegment(sketch, "E387", {"start": v(-1.15, -3.54) * mm, "end": v(-1.16, -3.56) * mm});
            skLineSegment(sketch, "E388", {"start": v(-1.15, -3.53) * mm, "end": v(-1.15, -3.54) * mm});
            skLineSegment(sketch, "E389", {"start": v(-1.14, -3.52) * mm, "end": v(-1.15, -3.53) * mm});
            skLineSegment(sketch, "E390", {"start": v(-1.14, -3.52) * mm, "end": v(-1.14, -3.52) * mm});
            skLineSegment(sketch, "E391", {"start": v(-0.99, -3.04) * mm, "end": v(-1.14, -3.52) * mm});
            skLineSegment(sketch, "E392", {"start": v(-0.24, -3.18) * mm, "end": v(-0.99, -3.04) * mm});
            skLineSegment(sketch, "E393", {"start": v(-0.28, -3.69) * mm, "end": v(-0.24, -3.18) * mm});
            skLineSegment(sketch, "E394", {"start": v(-0.28, -3.7) * mm, "end": v(-0.28, -3.69) * mm});
            skLineSegment(sketch, "E395", {"start": v(-0.28, -3.7) * mm, "end": v(-0.28, -3.7) * mm});
            skLineSegment(sketch, "E396", {"start": v(-0.28, -3.71) * mm, "end": v(-0.28, -3.7) * mm});
            skLineSegment(sketch, "E397", {"start": v(-0.28, -3.73) * mm, "end": v(-0.28, -3.71) * mm});
            skLineSegment(sketch, "E398", {"start": v(-0.27, -3.75) * mm, "end": v(-0.28, -3.73) * mm});
            skLineSegment(sketch, "E399", {"start": v(-0.27, -3.78) * mm, "end": v(-0.27, -3.75) * mm});
            skLineSegment(sketch, "E400", {"start": v(-0.27, -3.81) * mm, "end": v(-0.27, -3.78) * mm});
            skLineSegment(sketch, "E401", {"start": v(-0.26, -3.85) * mm, "end": v(-0.27, -3.81) * mm});
            skLineSegment(sketch, "E402", {"start": v(-0.25, -3.89) * mm, "end": v(-0.26, -3.85) * mm});
            skLineSegment(sketch, "E403", {"start": v(-0.24, -3.93) * mm, "end": v(-0.25, -3.89) * mm});
            skLineSegment(sketch, "E404", {"start": v(-0.22, -3.98) * mm, "end": v(-0.24, -3.93) * mm});
            skLineSegment(sketch, "E405", {"start": v(-0.2, -4.03) * mm, "end": v(-0.22, -3.98) * mm});
            skLineSegment(sketch, "E406", {"start": v(-0.18, -4.08) * mm, "end": v(-0.2, -4.03) * mm});
            skLineSegment(sketch, "E407", {"start": v(-0.16, -4.14) * mm, "end": v(-0.18, -4.08) * mm});
            skLineSegment(sketch, "E408", {"start": v(-0.13, -4.2) * mm, "end": v(-0.16, -4.14) * mm});
            skLineSegment(sketch, "E409", {"start": v(-0.1, -4.26) * mm, "end": v(-0.13, -4.2) * mm});
            skLineSegment(sketch, "E410", {"start": v(-0.05, -4.33) * mm, "end": v(-0.1, -4.26) * mm});
            skLineSegment(sketch, "E411", {"start": v(-0.01, -4.4) * mm, "end": v(-0.05, -4.33) * mm});
            skLineSegment(sketch, "E412", {"start": v(0.04, -4.47) * mm, "end": v(-0.01, -4.4) * mm});
            skLineSegment(sketch, "E413", {"start": v(0.09, -4.54) * mm, "end": v(0.04, -4.47) * mm});
            skLineSegment(sketch, "E414", {"start": v(0.15, -4.62) * mm, "end": v(0.09, -4.54) * mm});
            skLineSegment(sketch, "E415", {"start": v(0.2, -4.7) * mm, "end": v(0.15, -4.62) * mm});
            skLineSegment(sketch, "E416", {"start": v(0.28, -4.77) * mm, "end": v(0.2, -4.7) * mm});
            skLineSegment(sketch, "E417", {"start": v(0.35, -4.85) * mm, "end": v(0.28, -4.77) * mm});
            skLineSegment(sketch, "E418", {"start": v(0.43, -4.93) * mm, "end": v(0.35, -4.85) * mm});
            skLineSegment(sketch, "E419", {"start": v(0.51, -4.95) * mm, "end": v(0.43, -4.93) * mm});
            skLineSegment(sketch, "E420", {"start": v(0.67, -4.93) * mm, "end": v(0.51, -4.95) * mm});
            skLineSegment(sketch, "E421", {"start": v(0.75, -4.9) * mm, "end": v(0.67, -4.93) * mm});
            skLineSegment(sketch, "E422", {"start": v(0.8, -4.8) * mm, "end": v(0.75, -4.9) * mm});
            skLineSegment(sketch, "E423", {"start": v(0.86, -4.7) * mm, "end": v(0.8, -4.8) * mm});
            skLineSegment(sketch, "E424", {"start": v(0.9, -4.61) * mm, "end": v(0.86, -4.7) * mm});
            skLineSegment(sketch, "E425", {"start": v(0.95, -4.52) * mm, "end": v(0.9, -4.61) * mm});
            skLineSegment(sketch, "E426", {"start": v(1, -4.44) * mm, "end": v(0.95, -4.52) * mm});
            skLineSegment(sketch, "E427", {"start": v(1.02, -4.35) * mm, "end": v(1, -4.44) * mm});
            skLineSegment(sketch, "E428", {"start": v(1.05, -4.27) * mm, "end": v(1.02, -4.35) * mm});
            skLineSegment(sketch, "E429", {"start": v(1.08, -4.2) * mm, "end": v(1.05, -4.27) * mm});
            skLineSegment(sketch, "E430", {"start": v(1.1, -4.12) * mm, "end": v(1.08, -4.2) * mm});
            skLineSegment(sketch, "E431", {"start": v(1.12, -4.05) * mm, "end": v(1.1, -4.12) * mm});
            skLineSegment(sketch, "E432", {"start": v(1.13, -3.98) * mm, "end": v(1.12, -4.05) * mm});
            skLineSegment(sketch, "E433", {"start": v(1.14, -3.92) * mm, "end": v(1.13, -3.98) * mm});
            skLineSegment(sketch, "E434", {"start": v(1.15, -3.86) * mm, "end": v(1.14, -3.92) * mm});
            skLineSegment(sketch, "E435", {"start": v(1.16, -3.81) * mm, "end": v(1.15, -3.86) * mm});
            skLineSegment(sketch, "E436", {"start": v(1.16, -3.76) * mm, "end": v(1.16, -3.81) * mm});
            skLineSegment(sketch, "E437", {"start": v(1.16, -3.72) * mm, "end": v(1.16, -3.76) * mm});
            skLineSegment(sketch, "E438", {"start": v(1.16, -3.68) * mm, "end": v(1.16, -3.72) * mm});
            skLineSegment(sketch, "E439", {"start": v(1.16, -3.64) * mm, "end": v(1.16, -3.68) * mm});
            skLineSegment(sketch, "E440", {"start": v(1.16, -3.6) * mm, "end": v(1.16, -3.64) * mm});
            skLineSegment(sketch, "E441", {"start": v(1.15, -3.58) * mm, "end": v(1.16, -3.6) * mm});
            skLineSegment(sketch, "E442", {"start": v(1.15, -3.56) * mm, "end": v(1.15, -3.58) * mm});
            skLineSegment(sketch, "E443", {"start": v(1.15, -3.54) * mm, "end": v(1.15, -3.56) * mm});
            skLineSegment(sketch, "E444", {"start": v(1.15, -3.53) * mm, "end": v(1.15, -3.54) * mm});
            skLineSegment(sketch, "E445", {"start": v(1.14, -3.52) * mm, "end": v(1.15, -3.53) * mm});
            skLineSegment(sketch, "E446", {"start": v(1.14, -3.52) * mm, "end": v(1.14, -3.52) * mm});
            skLineSegment(sketch, "E447", {"start": v(0.99, -3.04) * mm, "end": v(1.14, -3.52) * mm});
            skLineSegment(sketch, "E448", {"start": v(1.68, -2.72) * mm, "end": v(0.99, -3.04) * mm});
            skLineSegment(sketch, "E449", {"start": v(1.94, -3.15) * mm, "end": v(1.68, -2.72) * mm});
            skLineSegment(sketch, "E450", {"start": v(1.94, -3.15) * mm, "end": v(1.94, -3.15) * mm});
            skLineSegment(sketch, "E451", {"start": v(1.95, -3.16) * mm, "end": v(1.94, -3.15) * mm});
            skLineSegment(sketch, "E452", {"start": v(1.96, -3.17) * mm, "end": v(1.95, -3.16) * mm});
            skLineSegment(sketch, "E453", {"start": v(1.97, -3.18) * mm, "end": v(1.96, -3.17) * mm});
            skLineSegment(sketch, "E454", {"start": v(1.98, -3.2) * mm, "end": v(1.97, -3.18) * mm});
            skLineSegment(sketch, "E455", {"start": v(2, -3.22) * mm, "end": v(1.98, -3.2) * mm});
            skLineSegment(sketch, "E456", {"start": v(2.03, -3.24) * mm, "end": v(2, -3.22) * mm});
            skLineSegment(sketch, "E457", {"start": v(2.05, -3.26) * mm, "end": v(2.03, -3.24) * mm});
            skLineSegment(sketch, "E458", {"start": v(2.08, -3.29) * mm, "end": v(2.05, -3.26) * mm});
            skLineSegment(sketch, "E459", {"start": v(2.12, -3.32) * mm, "end": v(2.08, -3.29) * mm});
            skLineSegment(sketch, "E460", {"start": v(2.16, -3.35) * mm, "end": v(2.12, -3.32) * mm});
            skLineSegment(sketch, "E461", {"start": v(2.2, -3.38) * mm, "end": v(2.16, -3.35) * mm});
            skLineSegment(sketch, "E462", {"start": v(2.25, -3.4) * mm, "end": v(2.2, -3.38) * mm});
            skLineSegment(sketch, "E463", {"start": v(2.3, -3.44) * mm, "end": v(2.25, -3.4) * mm});
            skLineSegment(sketch, "E464", {"start": v(2.37, -3.47) * mm, "end": v(2.3, -3.44) * mm});
            skLineSegment(sketch, "E465", {"start": v(2.43, -3.5) * mm, "end": v(2.37, -3.47) * mm});
            skLineSegment(sketch, "E466", {"start": v(2.5, -3.54) * mm, "end": v(2.43, -3.5) * mm});
            skLineSegment(sketch, "E467", {"start": v(2.58, -3.57) * mm, "end": v(2.5, -3.54) * mm});
            skLineSegment(sketch, "E468", {"start": v(2.66, -3.6) * mm, "end": v(2.58, -3.57) * mm});
            skLineSegment(sketch, "E469", {"start": v(2.74, -3.62) * mm, "end": v(2.66, -3.6) * mm});
            skLineSegment(sketch, "E470", {"start": v(2.83, -3.65) * mm, "end": v(2.74, -3.62) * mm});
            skLineSegment(sketch, "E471", {"start": v(2.93, -3.68) * mm, "end": v(2.83, -3.65) * mm});
            skLineSegment(sketch, "E472", {"start": v(3.03, -3.7) * mm, "end": v(2.93, -3.68) * mm});
            skLineSegment(sketch, "E473", {"start": v(3.14, -3.72) * mm, "end": v(3.03, -3.7) * mm});
            skLineSegment(sketch, "E474", {"start": v(3.25, -3.73) * mm, "end": v(3.14, -3.72) * mm});
            skLineSegment(sketch, "E475", {"start": v(3.33, -3.7) * mm, "end": v(3.25, -3.73) * mm});
            skLineSegment(sketch, "E476", {"start": v(3.44, -3.6) * mm, "end": v(3.33, -3.7) * mm});
            skLineSegment(sketch, "E477", {"start": v(3.48, -3.52) * mm, "end": v(3.44, -3.6) * mm});
            skLineSegment(sketch, "E478", {"start": v(3.47, -3.4) * mm, "end": v(3.48, -3.52) * mm});
            skLineSegment(sketch, "E479", {"start": v(3.46, -3.3) * mm, "end": v(3.47, -3.4) * mm});
            skLineSegment(sketch, "E480", {"start": v(3.45, -3.2) * mm, "end": v(3.46, -3.3) * mm});
            skLineSegment(sketch, "E481", {"start": v(3.43, -3.1) * mm, "end": v(3.45, -3.2) * mm});
            skLineSegment(sketch, "E482", {"start": v(3.4, -3) * mm, "end": v(3.43, -3.1) * mm});
            skLineSegment(sketch, "E483", {"start": v(3.39, -2.92) * mm, "end": v(3.4, -3) * mm});
            skLineSegment(sketch, "E484", {"start": v(3.36, -2.84) * mm, "end": v(3.39, -2.92) * mm});
            skLineSegment(sketch, "E485", {"start": v(3.34, -2.76) * mm, "end": v(3.36, -2.84) * mm});
            skLineSegment(sketch, "E486", {"start": v(3.31, -2.69) * mm, "end": v(3.34, -2.76) * mm});
            skLineSegment(sketch, "E487", {"start": v(3.28, -2.62) * mm, "end": v(3.31, -2.69) * mm});
            skLineSegment(sketch, "E488", {"start": v(3.26, -2.56) * mm, "end": v(3.28, -2.62) * mm});
            skLineSegment(sketch, "E489", {"start": v(3.23, -2.5) * mm, "end": v(3.26, -2.56) * mm});
            skLineSegment(sketch, "E490", {"start": v(3.2, -2.45) * mm, "end": v(3.23, -2.5) * mm});
            skLineSegment(sketch, "E491", {"start": v(3.18, -2.4) * mm, "end": v(3.2, -2.45) * mm});
            skLineSegment(sketch, "E492", {"start": v(3.15, -2.36) * mm, "end": v(3.18, -2.4) * mm});
            skLineSegment(sketch, "E493", {"start": v(3.12, -2.32) * mm, "end": v(3.15, -2.36) * mm});
            skLineSegment(sketch, "E494", {"start": v(3.1, -2.3) * mm, "end": v(3.12, -2.32) * mm});
            skLineSegment(sketch, "E495", {"start": v(3.08, -2.26) * mm, "end": v(3.1, -2.3) * mm});
            skLineSegment(sketch, "E496", {"start": v(3.06, -2.24) * mm, "end": v(3.08, -2.26) * mm});
            skLineSegment(sketch, "E497", {"start": v(3.04, -2.22) * mm, "end": v(3.06, -2.24) * mm});
            skLineSegment(sketch, "E498", {"start": v(3.02, -2.2) * mm, "end": v(3.04, -2.22) * mm});
            skLineSegment(sketch, "E499", {"start": v(3.01, -2.2) * mm, "end": v(3.02, -2.2) * mm});
            skLineSegment(sketch, "E500", {"start": v(3, -2.18) * mm, "end": v(3.01, -2.2) * mm});
            skLineSegment(sketch, "E501", {"start": v(3, -2.18) * mm, "end": v(3, -2.18) * mm});
            skLineSegment(sketch, "E502", {"start": v(3, -2.17) * mm, "end": v(3, -2.18) * mm});
            skLineSegment(sketch, "E503", {"start": v(2.58, -1.88) * mm, "end": v(3, -2.17) * mm});
            skLineSegment(sketch, "E504", {"start": v(2.95, -1.21) * mm, "end": v(2.58, -1.88) * mm});
            skLineSegment(sketch, "E505", {"start": v(3.42, -1.4) * mm, "end": v(2.95, -1.21) * mm});
            skLineSegment(sketch, "E506", {"start": v(3.42, -1.4) * mm, "end": v(3.42, -1.4) * mm});
            skLineSegment(sketch, "E507", {"start": v(3.43, -1.4) * mm, "end": v(3.42, -1.4) * mm});
            skLineSegment(sketch, "E508", {"start": v(3.45, -1.41) * mm, "end": v(3.43, -1.4) * mm});
            skLineSegment(sketch, "E509", {"start": v(3.46, -1.42) * mm, "end": v(3.45, -1.41) * mm});
            skLineSegment(sketch, "E510", {"start": v(3.48, -1.42) * mm, "end": v(3.46, -1.42) * mm});
            skLineSegment(sketch, "E511", {"start": v(3.51, -1.43) * mm, "end": v(3.48, -1.42) * mm});
            skLineSegment(sketch, "E512", {"start": v(3.54, -1.43) * mm, "end": v(3.51, -1.43) * mm});
            skLineSegment(sketch, "E513", {"start": v(3.58, -1.43) * mm, "end": v(3.54, -1.43) * mm});
            skLineSegment(sketch, "E514", {"start": v(3.62, -1.44) * mm, "end": v(3.58, -1.43) * mm});
            skLineSegment(sketch, "E515", {"start": v(3.66, -1.44) * mm, "end": v(3.62, -1.44) * mm});
            skLineSegment(sketch, "E516", {"start": v(3.71, -1.44) * mm, "end": v(3.66, -1.44) * mm});
            skLineSegment(sketch, "E517", {"start": v(3.77, -1.44) * mm, "end": v(3.71, -1.44) * mm});
            skLineSegment(sketch, "E518", {"start": v(3.83, -1.43) * mm, "end": v(3.77, -1.44) * mm});
            skLineSegment(sketch, "E519", {"start": v(3.89, -1.43) * mm, "end": v(3.83, -1.43) * mm});
            skLineSegment(sketch, "E520", {"start": v(3.96, -1.42) * mm, "end": v(3.89, -1.43) * mm});
            skLineSegment(sketch, "E521", {"start": v(4.03, -1.4) * mm, "end": v(3.96, -1.42) * mm});
            skLineSegment(sketch, "E522", {"start": v(4.1, -1.4) * mm, "end": v(4.03, -1.4) * mm});
            skLineSegment(sketch, "E523", {"start": v(4.18, -1.37) * mm, "end": v(4.1, -1.4) * mm});
            skLineSegment(sketch, "E524", {"start": v(4.26, -1.35) * mm, "end": v(4.18, -1.37) * mm});
            skLineSegment(sketch, "E525", {"start": v(4.35, -1.32) * mm, "end": v(4.26, -1.35) * mm});
            skLineSegment(sketch, "E526", {"start": v(4.44, -1.29) * mm, "end": v(4.35, -1.32) * mm});
            skLineSegment(sketch, "E527", {"start": v(4.53, -1.25) * mm, "end": v(4.44, -1.29) * mm});
            skLineSegment(sketch, "E528", {"start": v(4.62, -1.21) * mm, "end": v(4.53, -1.25) * mm});
            skLineSegment(sketch, "E529", {"start": v(4.72, -1.16) * mm, "end": v(4.62, -1.21) * mm});
            skLineSegment(sketch, "E530", {"start": v(4.82, -1.11) * mm, "end": v(4.72, -1.16) * mm});
            skLineSegment(sketch, "E531", {"start": v(4.87, -1.04) * mm, "end": v(4.82, -1.11) * mm});
            skLineSegment(sketch, "E532", {"start": v(4.9, -0.88) * mm, "end": v(4.87, -1.04) * mm});
            skLineSegment(sketch, "E533", {"start": v(4.88, -0.8) * mm, "end": v(4.9, -0.88) * mm});
            skLineSegment(sketch, "E534", {"start": v(4.8, -0.72) * mm, "end": v(4.88, -0.8) * mm});
            skLineSegment(sketch, "E535", {"start": v(4.74, -0.64) * mm, "end": v(4.8, -0.72) * mm});
            skLineSegment(sketch, "E536", {"start": v(4.67, -0.56) * mm, "end": v(4.74, -0.64) * mm});
            skLineSegment(sketch, "E537", {"start": v(4.6, -0.5) * mm, "end": v(4.67, -0.56) * mm});
            skLineSegment(sketch, "E538", {"start": v(4.52, -0.43) * mm, "end": v(4.6, -0.5) * mm});
            skLineSegment(sketch, "E539", {"start": v(4.46, -0.37) * mm, "end": v(4.52, -0.43) * mm});
            skLineSegment(sketch, "E540", {"start": v(4.39, -0.32) * mm, "end": v(4.46, -0.37) * mm});
            skLineSegment(sketch, "E541", {"start": v(4.32, -0.27) * mm, "end": v(4.39, -0.32) * mm});
            skLineSegment(sketch, "E542", {"start": v(4.26, -0.23) * mm, "end": v(4.32, -0.27) * mm});
            skLineSegment(sketch, "E543", {"start": v(4.2, -0.19) * mm, "end": v(4.26, -0.23) * mm});
            skLineSegment(sketch, "E544", {"start": v(4.14, -0.16) * mm, "end": v(4.2, -0.19) * mm});
            skLineSegment(sketch, "E545", {"start": v(4.08, -0.13) * mm, "end": v(4.14, -0.16) * mm});
            skLineSegment(sketch, "E546", {"start": v(4.03, -0.1) * mm, "end": v(4.08, -0.13) * mm});
            skLineSegment(sketch, "E547", {"start": v(3.98, -0.08) * mm, "end": v(4.03, -0.1) * mm});
            skLineSegment(sketch, "E548", {"start": v(3.94, -0.06) * mm, "end": v(3.98, -0.08) * mm});
            skLineSegment(sketch, "E549", {"start": v(3.9, -0.04) * mm, "end": v(3.94, -0.06) * mm});
            skLineSegment(sketch, "E550", {"start": v(3.85, -0.03) * mm, "end": v(3.9, -0.04) * mm});
            skLineSegment(sketch, "E551", {"start": v(3.82, -0.02) * mm, "end": v(3.85, -0.03) * mm});
            skLineSegment(sketch, "E552", {"start": v(3.79, -0.01) * mm, "end": v(3.82, -0.02) * mm});
            skLineSegment(sketch, "E553", {"start": v(3.76, 0) * mm, "end": v(3.79, -0.01) * mm});
            skLineSegment(sketch, "E554", {"start": v(3.74, 0) * mm, "end": v(3.76, 0) * mm});
            skLineSegment(sketch, "E555", {"start": v(3.72, 0) * mm, "end": v(3.74, 0) * mm});
            skLineSegment(sketch, "E556", {"start": v(3.7, 0) * mm, "end": v(3.72, 0) * mm});
            skLineSegment(sketch, "E557", {"start": v(3.7, 0) * mm, "end": v(3.7, 0) * mm});
            skLineSegment(sketch, "E558", {"start": v(3.2, 0) * mm, "end": v(3.7, 0) * mm});
            skLineSegment(sketch, "E559", {"start": v(3.1, 0.76) * mm, "end": v(3.2, 0) * mm});
            skSolve(sketch);
        }
        {
            var Q0;
            Q0=makeQuery(id+"F0.imprint","IMPRINT",FACE,{"disambiguationData":[TD([[makeQuery(id+"F0.imprint","IMPRINT",EDGE,{"derivedFrom":sQuery(id+"F0.wireOp",EDGE,"E0")}),-1.0]])]});
            extrude(context, id + "F1", {"entities" : qUnion([Q0]), "endBound" : BoundingType.SYMMETRIC, "depth" : 13 * mm});
        }
        {
            var Q0;
            Q0=qCreatedBy(makeId("Right.planeOp"),FACE);
            var sketch = newSketch(context, id + "F2", { "sketchPlane" : qUnion([Q0])});
            skLineSegment(sketch, "E560", {"start": v(6.5, 0) * mm, "end": v(-6.5, 0) * mm, "construction": true});
            skLineSegment(sketch, "E561", {"start": v(-3.5, 0) * mm, "end": v(-3.5, 5.2) * mm, "construction": true});
            skLineSegment(sketch, "E562", {"start": v(3.5, 0) * mm, "end": v(3.5, 6) * mm});
            skCircle(sketch, "E563", {"center": v(-3.5, 8.1) * mm, "radius": 2.9 * mm});
            skLineSegment(sketch, "E564", {"start": v(-3.5, 8.1) * mm, "end": v(-3.5, 5.2) * mm, "construction": true});
            skLineSegment(sketch, "E565", {"start": v(-5.5, 6) * mm, "end": v(-1.5, 6) * mm, "construction": true});
            skSolve(sketch);
        }
        {
            var Q0;
            Q0=makeQuery(id+"F2.imprint","IMPRINT",FACE,{"disambiguationData":[TD([[makeQuery(id+"F2.imprint","IMPRINT",EDGE,{"derivedFrom":sQuery(id+"F2.wireOp",EDGE,"E563")}),1.0]])]});
            var Q1;
            Q1=sQuery(id+"F2.wireOp",EDGE,"E560");
            revolve(context, id + "F3", {"operationType" : NewBodyOperationType.REMOVE, "entities" : qUnion([Q0]), "axis" : qUnion([Q1]), "revolveType" : RevolveType.FULL, "oppositeDirection" : true});
        }
        {
            var Q0;
            Q0=sQuery(id+"F2.wireOp",VERTEX,"E562.end");
            var Q1;
            Q1=sQuery(id+"F2.wireOp",EDGE,"E562");
            cPlane(context, id + "F4", {"entities" : qUnion([Q0, Q1]), "cplaneType" : CPlaneType.LINE_POINT, "offset" : 25 * mm, "width" : 150 * mm, "height" : 150 * mm});
        }
    });
